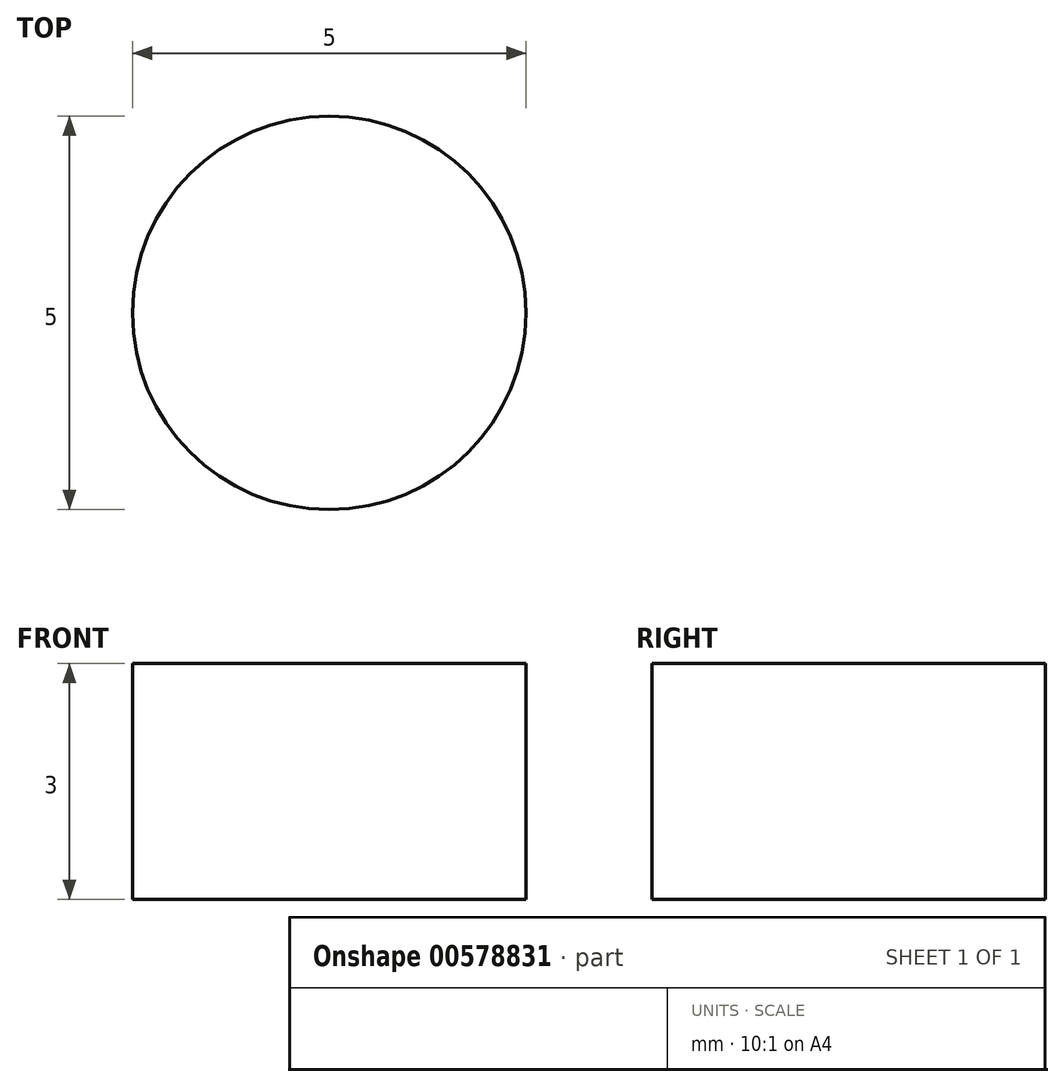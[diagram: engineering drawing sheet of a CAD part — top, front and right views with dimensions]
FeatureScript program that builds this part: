
annotation { "Feature Type Name" : "Feature", "Feature Type Description" : "" }
export const myFeature = defineFeature(function(context is Context, id is Id, definition is map)
    precondition{}
    {
        {
            var Q0;
            Q0=qCreatedBy(makeId("Top.planeOp"),FACE);
            var sketch = newSketch(context, id + "F0", { "sketchPlane" : qUnion([Q0])});
            skCircle(sketch, "E0", {"center": v(0, 0) * mm, "radius": 2.5 * mm});
            skSolve(sketch);
        }
        {
            var Q0;
            Q0 = qSketchRegion(id + "F0", true);
            extrude(context, id + "F1", {"entities" : qUnion([Q0]), "depth" : 3 * mm, "offsetDistance" : 25 * mm});
        }
    });
